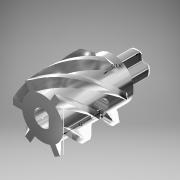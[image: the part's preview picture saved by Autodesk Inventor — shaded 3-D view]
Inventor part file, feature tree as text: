
AUTODESK INVENTOR PART (.ipt)
format: ipt  version: 2016 (Build 200138000, 138)  size: 530,944 bytes
history: native  units: mm
features: sketch x10, extrude x4, other x3, hole x3, plane x2, fillet x2, revolve x1, loft x1, sweep x1, chamfer x1, pattern_circular x1, projected_geometry x1
ambient origin geometry x8: Origin, YZ Plane, XZ Plane, XY Plane, X Axis, Y Axis, Z Axis, Center Point
bodies: Solid1 (feature_tree)
feature tree (30):
  extrude  "Extrusion1"  Depth=20.0mm TaperAngle=0.0deg
  other  "Work Axis1"
  plane  "Work Plane1"
  extrude  "Extrusion2"  Depth=3.0mm TaperAngle=0.0deg
  extrude  "Extrusion3"  Depth=2.7mm
  revolve  "Revolution1"  [1 undecoded]
  fillet  "Fillet6"  Radius=8.6mm
  fillet  "Fillet2"  Radius=0.4mm
  plane  "Work Plane2"
  sketch  "Sketch7"  dims[d38=1.5mm d43=12.0mm]
  loft  "Loft2"
  hole  "Hole1"  [1 undecoded]
  extrude  "Extrusion5"  TaperAngle=0.0deg  [1 undecoded]
  sweep  "Sweep1"
  chamfer  "Chamfer1"  Distance=10.0mm
  pattern_circular  "Circular Pattern1"  [2 undecoded]
  sketch  "Sketch2"  dims[d90=10.0mm d91=10.0mm d5=5.4mm d6=6.0mm d7=4.0mm d8=2.0mm d9=90.0deg d10=20.0mm d11=20.594885mm]
  hole  "Hole2"  [1 undecoded]
  hole  "Hole3"  [1 undecoded]
  sketch  "Sketch14"  dims[d52=1.4mm d57=23.5mm d70=10.0mm d71=0.0mm d75=2.02mm d76=2.0mm d77=3.0mm d78=60.0mm d79=20.0mm d80=13.5mm d81=0.0mm d82=0.0mm d83=0.0mm d84=60.0mm d85=360.0deg d87=2.0mm d88=12.0mm d89=45.0deg d92=6.0mm d93=6.0mm d94=4.0mm d95=2.0mm d96=90.0deg d97=8.0mm d98=20.594885mm d55=1.0mm d56=1.0mm]
  sketch  "Sketch1"  dims[d0=13.5mm d1=20.0mm d2=0.0mm]
  sketch  "Sketch3"  dims[d13=6.75mm d14=5.2mm d15=6.0mm d16=6.0mm d17=2.0mm d18=90.0deg d19=13.5mm d20=20.594885mm d23=3.0mm d24=0.0mm]
  sketch  "Sketch4"  dims[d25=2.7mm d26=2.7mm]
  sketch  "Sketch6"  dims[d27=9.0mm d28=9.0mm d29=8.6mm d30=0.0mm d32=0.4mm]
  projected_geometry  "Projected Loop2"
  other  "Edges2"
  sketch  "Sketch11"  dims[d44=90.0deg d47=0.6mm]
  sketch  "Sketch12"  dims[d48=0.0mm d49=90.0deg d50=0.0mm d51=90.0deg]
  sketch  "3D Sketch1"
  other  "Helical Curve1"
note: 7 required parameter values undecoded (feature->parameter linkage not recoverable at this tier; creation-order binding heuristic only, values carry confidence <= 0.55)